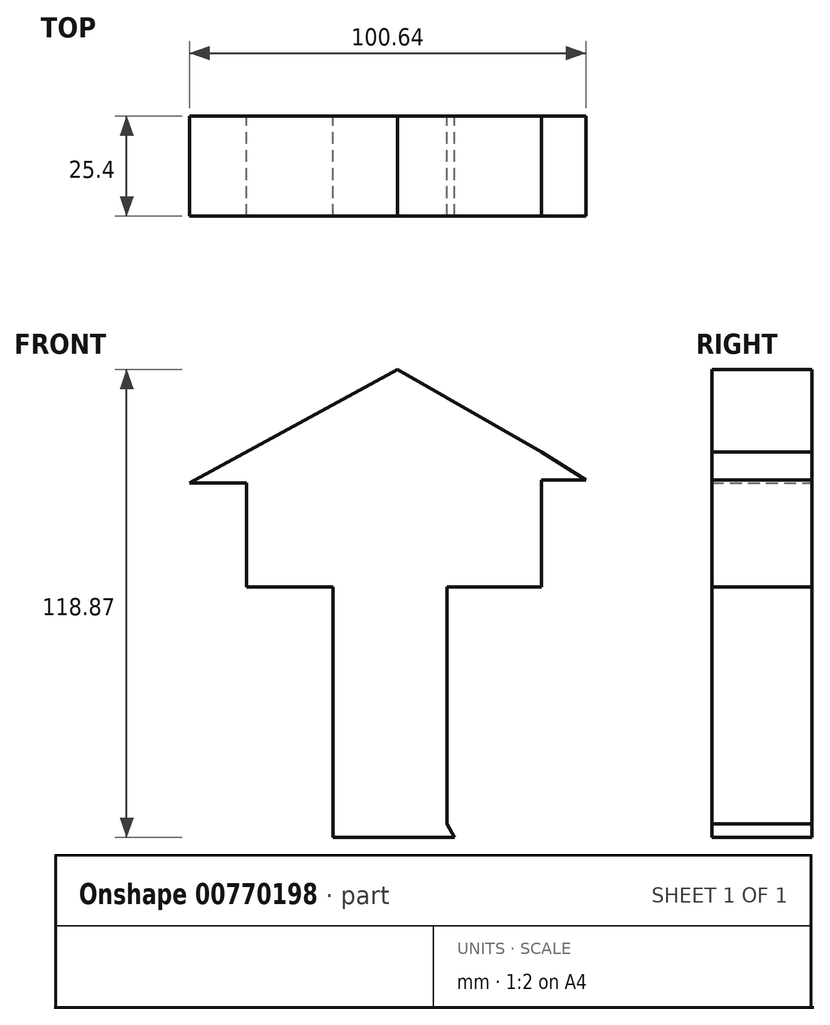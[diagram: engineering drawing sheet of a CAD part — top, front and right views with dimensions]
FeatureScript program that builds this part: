
annotation { "Feature Type Name" : "Feature", "Feature Type Description" : "" }
export const myFeature = defineFeature(function(context is Context, id is Id, definition is map)
    precondition{}
    {
        {
            var Q0;
            Q0=qCreatedBy(makeId("Front.planeOp"),FACE);
            var sketch = newSketch(context, id + "F0", { "sketchPlane" : qUnion([Q0])});
            skLineSegment(sketch, "E0", {"start": v(0, 55.27) * mm, "end": v(-38.28, 34.38) * mm});
            skLineSegment(sketch, "E1", {"start": v(-38.28, 34.38) * mm, "end": v(36.62, 34.38) * mm});
            skLineSegment(sketch, "E2", {"start": v(0, 55.27) * mm, "end": v(36.62, 34.38) * mm});
            skLineSegment(sketch, "E3", {"start": v(-38.28, 34.38) * mm, "end": v(-52.74, 26.5) * mm});
            skLineSegment(sketch, "E4", {"start": v(36, 34.03) * mm, "end": v(47.9, 27.24) * mm});
            skLineSegment(sketch, "E5", {"start": v(-17.94, 34.38) * mm, "end": v(-29.71, 34.38) * mm});
            skLineSegment(sketch, "E6", {"start": v(-29.71, 0) * mm, "end": v(36.62, 0) * mm});
            skLineSegment(sketch, "E7", {"start": v(36.62, 0) * mm, "end": v(36.62, 34.38) * mm});
            skLineSegment(sketch, "E8", {"start": v(47.9, 27.24) * mm, "end": v(36.62, 27.24) * mm});
            skLineSegment(sketch, "E9", {"start": v(-38.28, 34.38) * mm, "end": v(-38.28, 0) * mm});
            skLineSegment(sketch, "E10", {"start": v(-38.28, 0) * mm, "end": v(-29.71, 0) * mm});
            skLineSegment(sketch, "E11", {"start": v(-16.38, 0) * mm, "end": v(-16.38, -57.9) * mm});
            skLineSegment(sketch, "E12", {"start": v(12.65, 0) * mm, "end": v(12.65, -60.18) * mm});
            skLineSegment(sketch, "E13", {"start": v(-16.38, -57.9) * mm, "end": v(-16.38, -63.6) * mm});
            skLineSegment(sketch, "E14", {"start": v(-16.38, -63.6) * mm, "end": v(15.2, -63.6) * mm});
            skLineSegment(sketch, "E15", {"start": v(15.2, -64.86) * mm, "end": v(12.65, -60.18) * mm});
            skPoint(sketch, "E16.orphan", {"position": v(-29.71, 17.2) * mm});
            skPoint(sketch, "E17.orphan", {"position": v(-29.71, 26.5) * mm});
            skLineSegment(sketch, "E18", {"start": v(-52.74, 26.5) * mm, "end": v(-38.28, 26.5) * mm});
            skLineSegment(sketch, "E19", {"start": v(36.62, 34.38) * mm, "end": v(47.9, 27.24) * mm});
            skSolve(sketch);
        }
        {
            var Q0;
            Q0 = qSketchRegion(id + "F0", true);
            extrude(context, id + "F1", {"entities" : qUnion([Q0]), "depth" : 25.4 * mm, "offsetDistance" : 25.4 * mm});
        }
    });
